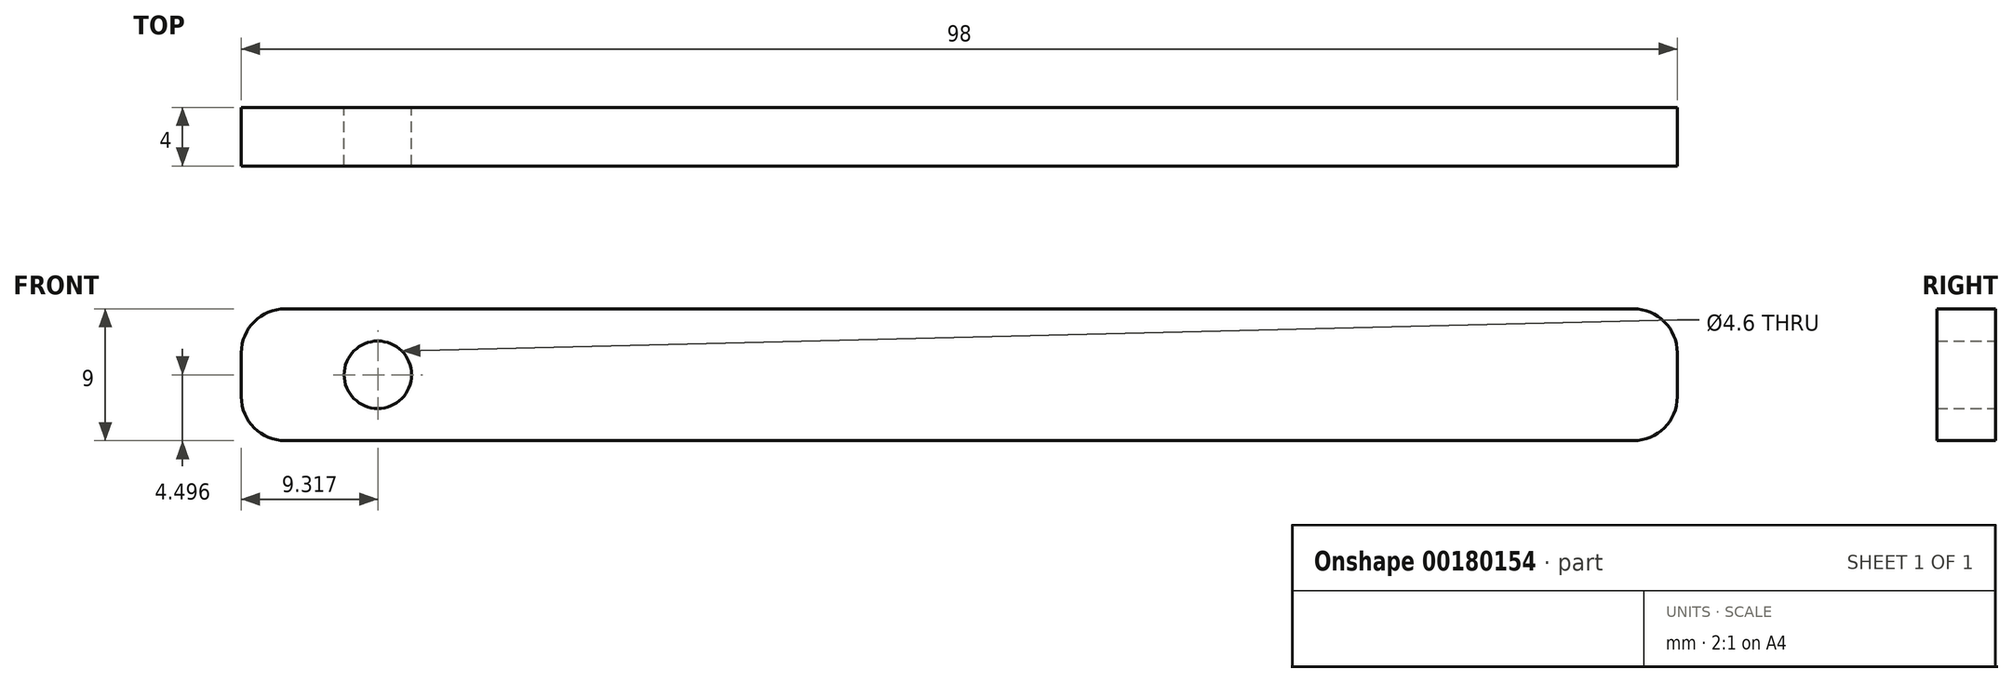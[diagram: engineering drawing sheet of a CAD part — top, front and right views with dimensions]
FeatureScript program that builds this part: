
annotation { "Feature Type Name" : "Feature", "Feature Type Description" : "" }
export const myFeature = defineFeature(function(context is Context, id is Id, definition is map)
    precondition{}
    {
        {
            var Q0;
            Q0=qCreatedBy(makeId("Front.planeOp"),FACE);
            var sketch = newSketch(context, id + "F0", { "sketchPlane" : qUnion([Q0])});
            skLineSegment(sketch, "E0", {"start": v(-65.27, 35.5) * mm, "end": v(26.73, 35.5) * mm});
            skLineSegment(sketch, "E1", {"start": v(29.73, 32.5) * mm, "end": v(29.73, 29.5) * mm});
            skLineSegment(sketch, "E2", {"start": v(26.73, 26.5) * mm, "end": v(-65.27, 26.5) * mm});
            skLineSegment(sketch, "E3", {"start": v(-68.27, 29.5) * mm, "end": v(-68.27, 32.5) * mm});
            skCircle(sketch, "E4", {"center": v(-58.95, 31) * mm, "radius": 2.3 * mm});
            skPoint(sketch, "E4.centerSnap0", {"position": v(-68.27, 31) * mm});
            skPoint(sketch, "E5.visualSharp", {"position": v(-68.27, 35.5) * mm});
            skArc(sketch, "E5.filletArc", {"start": v(-65.27, 35.5) * mm, "mid": v(-67.4, 34.62) * mm, "end": v(-68.27, 32.5) * mm});
            skPoint(sketch, "E6.visualSharp", {"position": v(-68.27, 26.5) * mm});
            skArc(sketch, "E6.filletArc", {"start": v(-68.27, 29.5) * mm, "mid": v(-67.4, 27.37) * mm, "end": v(-65.27, 26.5) * mm});
            skPoint(sketch, "E7.visualSharp", {"position": v(29.73, 35.5) * mm});
            skArc(sketch, "E7.filletArc", {"start": v(29.73, 32.5) * mm, "mid": v(28.85, 34.62) * mm, "end": v(26.73, 35.5) * mm});
            skPoint(sketch, "E8.visualSharp", {"position": v(29.73, 26.5) * mm});
            skArc(sketch, "E8.filletArc", {"start": v(26.73, 26.5) * mm, "mid": v(28.85, 27.37) * mm, "end": v(29.73, 29.5) * mm});
            skSolve(sketch);
        }
        {
            var Q0;
            Q0 = qSketchRegion(id + "F0", true);
            extrude(context, id + "F1", {"entities" : qUnion([Q0]), "depth" : 4 * mm});
        }
    });
